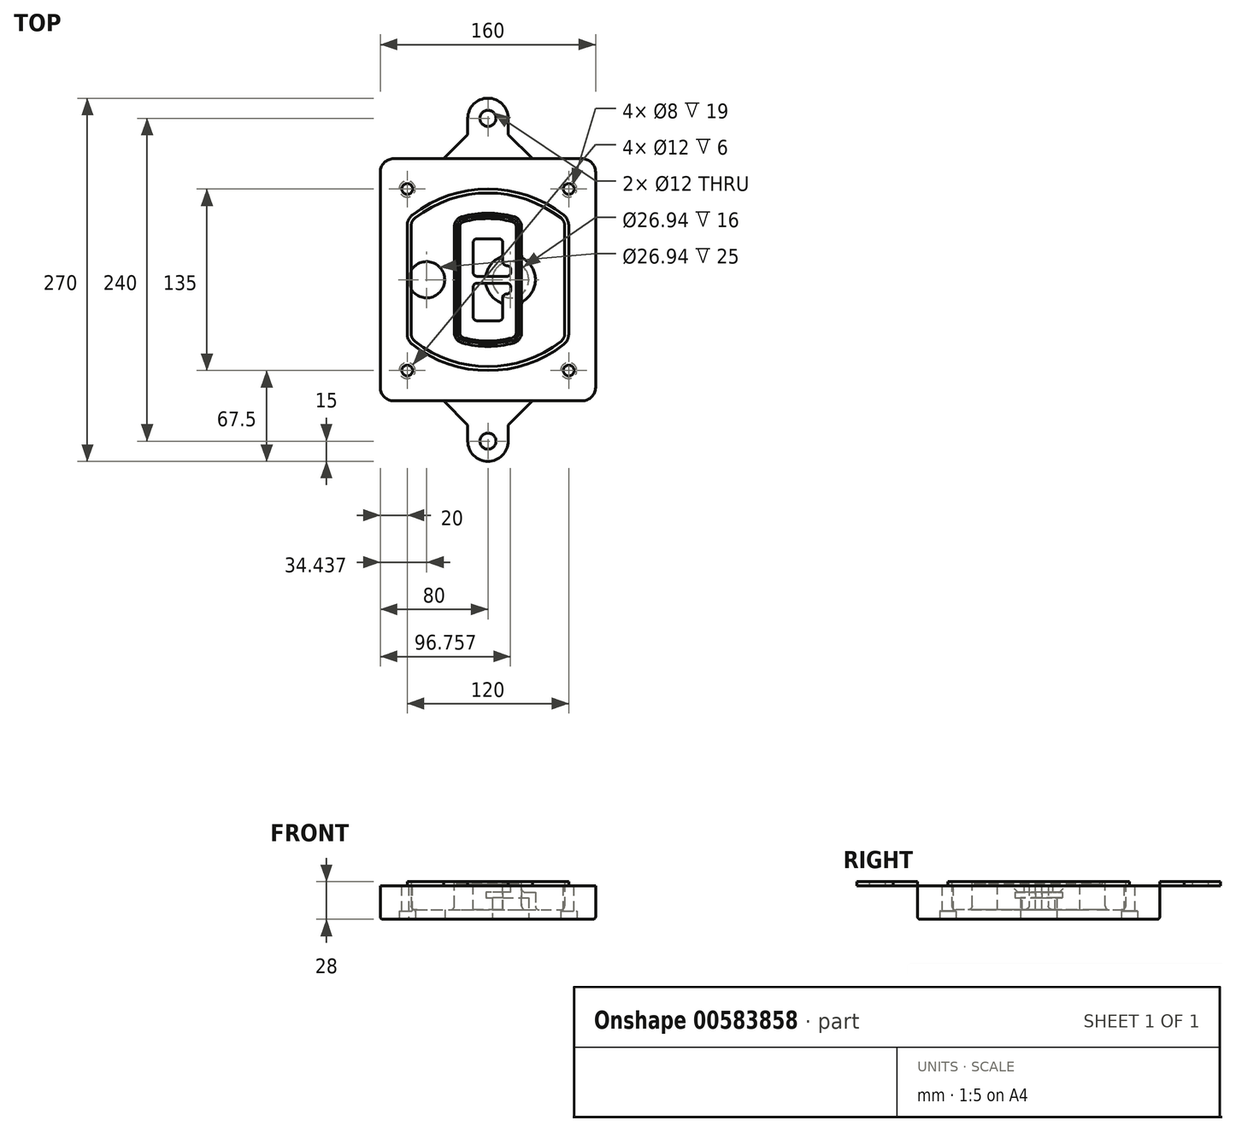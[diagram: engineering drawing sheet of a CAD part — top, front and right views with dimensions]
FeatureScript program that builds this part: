
annotation { "Feature Type Name" : "Feature", "Feature Type Description" : "" }
export const myFeature = defineFeature(function(context is Context, id is Id, definition is map)
    precondition{}
    {
        {
            var Q0;
            Q0=qCreatedBy(makeId("Top.planeOp"),FACE);
            var sketch = newSketch(context, id + "F0", { "sketchPlane" : qUnion([Q0])});
            skPoint(sketch, "E0.rect.middle", {"position": v(0, 0) * mm});
            skLineSegment(sketch, "E1.bottom", {"start": v(-70, -90) * mm, "end": v(70, -90) * mm});
            skLineSegment(sketch, "E1.top", {"start": v(-70, 90) * mm, "end": v(70, 90) * mm});
            skLineSegment(sketch, "E1.left", {"start": v(-80, -80) * mm, "end": v(-80, 80) * mm});
            skLineSegment(sketch, "E1.right", {"start": v(80, -80) * mm, "end": v(80, 80) * mm});
            skLineSegment(sketch, "E2", {"start": v(-80, 90) * mm, "end": v(80, -90) * mm, "construction": true});
            skLineSegment(sketch, "E3", {"start": v(80, 90) * mm, "end": v(-80, -90) * mm, "construction": true});
            skCircle(sketch, "E4", {"center": v(-60, 67.5) * mm, "radius": 4 * mm});
            skCircle(sketch, "E5", {"center": v(60, 67.5) * mm, "radius": 4 * mm});
            skCircle(sketch, "E6", {"center": v(60, -67.5) * mm, "radius": 4 * mm});
            skCircle(sketch, "E7", {"center": v(-60, -67.5) * mm, "radius": 4 * mm});
            skLineSegment(sketch, "E8", {"start": v(-60, 67.5) * mm, "end": v(60, 67.5) * mm, "construction": true});
            skLineSegment(sketch, "E9", {"start": v(60, 67.5) * mm, "end": v(60, -67.5) * mm, "construction": true});
            skLineSegment(sketch, "E10", {"start": v(60, -67.5) * mm, "end": v(-60, -67.5) * mm, "construction": true});
            skLineSegment(sketch, "E11", {"start": v(-60, -67.5) * mm, "end": v(-60, 67.5) * mm, "construction": true});
            skLineSegment(sketch, "E12", {"start": v(-60, 40.3) * mm, "end": v(-60, -40.3) * mm});
            skLineSegment(sketch, "E13", {"start": v(60, 40.3) * mm, "end": v(60, -40.3) * mm});
            skArc(sketch, "E14", {"start": v(56.15, 48.18) * mm, "mid": v(0, 67.5) * mm, "end": v(-56.15, 48.18) * mm});
            skArc(sketch, "E15", {"start": v(-56.15, -48.18) * mm, "mid": v(0, -67.5) * mm, "end": v(56.15, -48.18) * mm});
            skLineSegment(sketch, "E16", {"start": v(-60, 0) * mm, "end": v(60, 0) * mm, "construction": true});
            skPoint(sketch, "E17.visualSharp", {"position": v(-60, -45) * mm});
            skArc(sketch, "E17.filletArc", {"start": v(-60, -40.3) * mm, "mid": v(-58.99, -44.68) * mm, "end": v(-56.15, -48.18) * mm});
            skPoint(sketch, "E18.visualSharp", {"position": v(-60, 45) * mm});
            skArc(sketch, "E18.filletArc", {"start": v(-56.15, 48.18) * mm, "mid": v(-58.99, 44.68) * mm, "end": v(-60, 40.3) * mm});
            skPoint(sketch, "E19.visualSharp", {"position": v(60, 45) * mm});
            skArc(sketch, "E19.filletArc", {"start": v(60, 40.3) * mm, "mid": v(58.99, 44.68) * mm, "end": v(56.15, 48.18) * mm});
            skPoint(sketch, "E20.visualSharp", {"position": v(60, -45) * mm});
            skArc(sketch, "E20.filletArc", {"start": v(56.15, -48.18) * mm, "mid": v(58.99, -44.68) * mm, "end": v(60, -40.3) * mm});
            skPoint(sketch, "E21.visualSharp", {"position": v(-80, 90) * mm});
            skArc(sketch, "E21.filletArc", {"start": v(-70, 90) * mm, "mid": v(-77.07, 87.07) * mm, "end": v(-80, 80) * mm});
            skPoint(sketch, "E22.visualSharp", {"position": v(80, 90) * mm});
            skArc(sketch, "E22.filletArc", {"start": v(80, 80) * mm, "mid": v(77.07, 87.07) * mm, "end": v(70, 90) * mm});
            skPoint(sketch, "E23.visualSharp", {"position": v(80, -90) * mm});
            skArc(sketch, "E23.filletArc", {"start": v(70, -90) * mm, "mid": v(77.07, -87.07) * mm, "end": v(80, -80) * mm});
            skPoint(sketch, "E24.visualSharp", {"position": v(-80, -90) * mm});
            skArc(sketch, "E24.filletArc", {"start": v(-80, -80) * mm, "mid": v(-77.07, -87.07) * mm, "end": v(-70, -90) * mm});
            skArc(sketch, "E25.0", {"start": v(57, 40.3) * mm, "mid": v(56.3, 43.36) * mm, "end": v(54.3, 45.81) * mm});
            skLineSegment(sketch, "E25.1", {"start": v(57, 40.3) * mm, "end": v(57, -40.3) * mm});
            skArc(sketch, "E25.2", {"start": v(54.3, -45.81) * mm, "mid": v(56.3, -43.36) * mm, "end": v(57, -40.3) * mm});
            skArc(sketch, "E25.3", {"start": v(-54.3, -45.81) * mm, "mid": v(0, -64.5) * mm, "end": v(54.3, -45.81) * mm});
            skArc(sketch, "E25.4", {"start": v(-57, -40.3) * mm, "mid": v(-56.3, -43.36) * mm, "end": v(-54.3, -45.81) * mm});
            skArc(sketch, "E25.5", {"start": v(54.3, 45.81) * mm, "mid": v(0, 64.5) * mm, "end": v(-54.3, 45.81) * mm});
            skLineSegment(sketch, "E25.6", {"start": v(-57, 40.3) * mm, "end": v(-57, -40.3) * mm});
            skArc(sketch, "E25.7", {"start": v(-54.3, 45.81) * mm, "mid": v(-56.3, 43.36) * mm, "end": v(-57, 40.3) * mm});
            skArc(sketch, "E26.0", {"start": v(-58.62, 51.33) * mm, "mid": v(-62.58, 46.43) * mm, "end": v(-64, 40.3) * mm});
            skArc(sketch, "E26.1", {"start": v(58.62, 51.33) * mm, "mid": v(0, 71.5) * mm, "end": v(-58.62, 51.33) * mm});
            skArc(sketch, "E26.2", {"start": v(64, 40.3) * mm, "mid": v(62.58, 46.43) * mm, "end": v(58.62, 51.33) * mm});
            skLineSegment(sketch, "E26.3", {"start": v(64, 40.3) * mm, "end": v(64, -40.3) * mm});
            skArc(sketch, "E26.4", {"start": v(58.62, -51.33) * mm, "mid": v(62.58, -46.43) * mm, "end": v(64, -40.3) * mm});
            skLineSegment(sketch, "E26.5", {"start": v(-64, 40.3) * mm, "end": v(-64, -40.3) * mm});
            skArc(sketch, "E26.6", {"start": v(-58.62, -51.33) * mm, "mid": v(0, -71.5) * mm, "end": v(58.62, -51.33) * mm});
            skArc(sketch, "E26.7", {"start": v(-64, -40.3) * mm, "mid": v(-62.58, -46.43) * mm, "end": v(-58.62, -51.33) * mm});
            skSolve(sketch);
        }
        {
            var Q0;
            Q0=makeQuery(id+"F0.imprint","IMPRINT",FACE,{"disambiguationData":[TD([[makeQuery(id+"F0.imprint","IMPRINT",EDGE,{"derivedFrom":sQuery(id+"F0.wireOp",EDGE,"E1.bottom")}),1.0]])]});
            var Q1;
            Q1=makeQuery(id+"F0.imprint","IMPRINT",FACE,{"disambiguationData":[TD([[makeQuery(id+"F0.imprint","IMPRINT",EDGE,{"derivedFrom":sQuery(id+"F0.wireOp",EDGE,"E12")}),1.0]])]});
            var Q2;
            Q2=makeQuery(id+"F0.imprint","IMPRINT",FACE,{"disambiguationData":[TD([[makeQuery(id+"F0.imprint","IMPRINT",EDGE,{"derivedFrom":sQuery(id+"F0.wireOp",EDGE,"E25.0")}),1.0]])]});
            var Q3;
            Q3=makeQuery(id+"F0.imprint","IMPRINT",FACE,{"disambiguationData":[TD([[makeQuery(id+"F0.imprint","IMPRINT",EDGE,{"derivedFrom":sQuery(id+"F0.wireOp",EDGE,"E12")}),-1.0]])]});
            extrude(context, id + "F1", {"entities" : qUnion([Q0, Q1, Q2, Q3]), "oppositeDirection" : true, "depth" : 25 * mm});
        }
        {
            var Q0;
            Q0=makeQuery(id+"F0.imprint","IMPRINT",FACE,{"disambiguationData":[TD([[makeQuery(id+"F0.imprint","IMPRINT",EDGE,{"derivedFrom":sQuery(id+"F0.wireOp",EDGE,"E12")}),1.0]])]});
            extrude(context, id + "F2", {"entities" : qUnion([Q0]), "operationType" : NewBodyOperationType.ADD, "depth" : 3 * mm});
        }
        {
            var Q0;
            Q0=makeQuery(id+"F0.imprint","IMPRINT",FACE,{"disambiguationData":[TD([[makeQuery(id+"F0.imprint","IMPRINT",EDGE,{"derivedFrom":sQuery(id+"F0.wireOp",EDGE,"E25.0")}),1.0]])]});
            extrude(context, id + "F3", {"entities" : qUnion([Q0]), "operationType" : NewBodyOperationType.REMOVE, "oppositeDirection" : true, "depth" : 18 * mm});
        }
        {
            var Q0;
            Q0=makeQuery(id+"F2.opExtrude","CAP_FACE",FACE,{"disambiguationData":[OSD([sQuery(id+"F0.wireOp",EDGE,"E12"),sQuery(id+"F0.wireOp",EDGE,"E13"),sQuery(id+"F0.wireOp",EDGE,"E14"),sQuery(id+"F0.wireOp",EDGE,"E15"),sQuery(id+"F0.wireOp",EDGE,"E17.filletArc"),sQuery(id+"F0.wireOp",EDGE,"E18.filletArc"),sQuery(id+"F0.wireOp",EDGE,"E19.filletArc"),sQuery(id+"F0.wireOp",EDGE,"E20.filletArc"),sQuery(id+"F0.wireOp",EDGE,"E25.0"),sQuery(id+"F0.wireOp",EDGE,"E25.1"),sQuery(id+"F0.wireOp",EDGE,"E25.2"),sQuery(id+"F0.wireOp",EDGE,"E25.3"),sQuery(id+"F0.wireOp",EDGE,"E25.4"),sQuery(id+"F0.wireOp",EDGE,"E25.5"),sQuery(id+"F0.wireOp",EDGE,"E25.6"),sQuery(id+"F0.wireOp",EDGE,"E25.7")])],"isStart":false});
            var sketch = newSketch(context, id + "F4", { "sketchPlane" : qUnion([Q0])});
            skArc(sketch, "E27.0", {"start": v(-19.08, -46.97) * mm, "mid": v(0, -49.5) * mm, "end": v(19.08, -46.97) * mm});
            skArc(sketch, "E28.0", {"start": v(19.08, 46.97) * mm, "mid": v(0, 49.5) * mm, "end": v(-19.08, 46.97) * mm});
            skLineSegment(sketch, "E29", {"start": v(-25, 39.25) * mm, "end": v(-25, -39.25) * mm});
            skLineSegment(sketch, "E30", {"start": v(25, 39.25) * mm, "end": v(25, -39.25) * mm});
            skLineSegment(sketch, "E31", {"start": v(-25, 45.1) * mm, "end": v(25, 45.1) * mm, "construction": true});
            skLineSegment(sketch, "E32", {"start": v(-25, -45.1) * mm, "end": v(25, -45.1) * mm, "construction": true});
            skPoint(sketch, "E33.visualSharp", {"position": v(-25, 45.1) * mm});
            skArc(sketch, "E33.filletArc", {"start": v(-19.08, 46.97) * mm, "mid": v(-23.35, 44.11) * mm, "end": v(-25, 39.25) * mm});
            skPoint(sketch, "E34.visualSharp", {"position": v(25, 45.1) * mm});
            skArc(sketch, "E34.filletArc", {"start": v(25, 39.25) * mm, "mid": v(23.35, 44.11) * mm, "end": v(19.08, 46.97) * mm});
            skPoint(sketch, "E35.visualSharp", {"position": v(25, -45.1) * mm});
            skArc(sketch, "E35.filletArc", {"start": v(19.08, -46.97) * mm, "mid": v(23.35, -44.11) * mm, "end": v(25, -39.25) * mm});
            skPoint(sketch, "E36.visualSharp", {"position": v(-25, -45.1) * mm});
            skArc(sketch, "E36.filletArc", {"start": v(-25, -39.25) * mm, "mid": v(-23.35, -44.11) * mm, "end": v(-19.08, -46.97) * mm});
            skArc(sketch, "E37.0", {"start": v(54.3, 45.81) * mm, "mid": v(0, 64.5) * mm, "end": v(-54.3, 45.81) * mm});
            skArc(sketch, "E37.1", {"start": v(-54.3, 45.81) * mm, "mid": v(-56.3, 43.36) * mm, "end": v(-57, 40.3) * mm});
            skLineSegment(sketch, "E37.2", {"start": v(-57, 40.3) * mm, "end": v(-57, -40.3) * mm});
            skArc(sketch, "E37.3", {"start": v(-57, -40.3) * mm, "mid": v(-56.3, -43.36) * mm, "end": v(-54.3, -45.81) * mm});
            skArc(sketch, "E37.4", {"start": v(-54.3, -45.81) * mm, "mid": v(0, -64.5) * mm, "end": v(54.3, -45.81) * mm});
            skArc(sketch, "E37.5", {"start": v(54.3, -45.81) * mm, "mid": v(56.3, -43.36) * mm, "end": v(57, -40.3) * mm});
            skLineSegment(sketch, "E37.6", {"start": v(57, 40.3) * mm, "end": v(57, -40.3) * mm});
            skArc(sketch, "E37.7", {"start": v(57, 40.3) * mm, "mid": v(56.3, 43.36) * mm, "end": v(54.3, 45.81) * mm});
            skLineSegment(sketch, "E38.0", {"start": v(23, 39.25) * mm, "end": v(23, -39.25) * mm});
            skArc(sketch, "E38.1", {"start": v(18.56, -45.04) * mm, "mid": v(21.76, -42.9) * mm, "end": v(23, -39.25) * mm});
            skArc(sketch, "E38.2", {"start": v(-18.56, -45.04) * mm, "mid": v(0, -47.5) * mm, "end": v(18.56, -45.04) * mm});
            skArc(sketch, "E38.3", {"start": v(-23, -39.25) * mm, "mid": v(-21.76, -42.9) * mm, "end": v(-18.56, -45.04) * mm});
            skLineSegment(sketch, "E38.4", {"start": v(-23, 39.25) * mm, "end": v(-23, -39.25) * mm});
            skArc(sketch, "E38.5", {"start": v(23, 39.25) * mm, "mid": v(21.76, 42.9) * mm, "end": v(18.56, 45.04) * mm});
            skArc(sketch, "E38.6", {"start": v(-18.56, 45.04) * mm, "mid": v(-21.76, 42.9) * mm, "end": v(-23, 39.25) * mm});
            skArc(sketch, "E38.7", {"start": v(18.56, 45.04) * mm, "mid": v(0, 47.5) * mm, "end": v(-18.56, 45.04) * mm});
            skArc(sketch, "E39.0", {"start": v(21, 39.25) * mm, "mid": v(20.18, 41.68) * mm, "end": v(18.04, 43.1) * mm});
            skLineSegment(sketch, "E39.1", {"start": v(21, 39.25) * mm, "end": v(21, -39.25) * mm});
            skArc(sketch, "E39.2", {"start": v(18.04, -43.1) * mm, "mid": v(20.18, -41.68) * mm, "end": v(21, -39.25) * mm});
            skArc(sketch, "E39.3", {"start": v(-18.04, -43.1) * mm, "mid": v(0, -45.5) * mm, "end": v(18.04, -43.1) * mm});
            skArc(sketch, "E39.4", {"start": v(-21, -39.25) * mm, "mid": v(-20.18, -41.68) * mm, "end": v(-18.04, -43.1) * mm});
            skArc(sketch, "E39.5", {"start": v(18.04, 43.1) * mm, "mid": v(0, 45.5) * mm, "end": v(-18.04, 43.1) * mm});
            skLineSegment(sketch, "E39.6", {"start": v(-21, 39.25) * mm, "end": v(-21, -39.25) * mm});
            skArc(sketch, "E39.7", {"start": v(-18.04, 43.1) * mm, "mid": v(-20.18, 41.68) * mm, "end": v(-21, 39.25) * mm});
            skLineSegment(sketch, "E40", {"start": v(-25, 0) * mm, "end": v(25, 0) * mm, "construction": true});
            skLineSegment(sketch, "E41", {"start": v(-11, 5.5) * mm, "end": v(-11, 27.5) * mm});
            skLineSegment(sketch, "E42", {"start": v(-8, 30.5) * mm, "end": v(8, 30.5) * mm});
            skLineSegment(sketch, "E43", {"start": v(11, 27.5) * mm, "end": v(11, 13.5) * mm});
            skLineSegment(sketch, "E44", {"start": v(14, 10.5) * mm, "end": v(14, 10.5) * mm});
            skLineSegment(sketch, "E45", {"start": v(17, 7.5) * mm, "end": v(17, 5.5) * mm});
            skLineSegment(sketch, "E46", {"start": v(14, 2.5) * mm, "end": v(-8, 2.5) * mm});
            skPoint(sketch, "E47.visualSharp", {"position": v(-11, 30.5) * mm});
            skArc(sketch, "E47.filletArc", {"start": v(-8, 30.5) * mm, "mid": v(-10.12, 29.62) * mm, "end": v(-11, 27.5) * mm});
            skPoint(sketch, "E48.visualSharp", {"position": v(11, 30.5) * mm});
            skArc(sketch, "E48.filletArc", {"start": v(11, 27.5) * mm, "mid": v(10.12, 29.62) * mm, "end": v(8, 30.5) * mm});
            skPoint(sketch, "E49.visualSharp", {"position": v(11, 10.5) * mm});
            skArc(sketch, "E49.filletArc", {"start": v(11, 13.5) * mm, "mid": v(11.88, 11.38) * mm, "end": v(14, 10.5) * mm});
            skPoint(sketch, "E50.visualSharp", {"position": v(17, 10.5) * mm});
            skArc(sketch, "E50.filletArc", {"start": v(17, 7.5) * mm, "mid": v(16.12, 9.62) * mm, "end": v(14, 10.5) * mm});
            skPoint(sketch, "E51.visualSharp", {"position": v(17, 2.5) * mm});
            skArc(sketch, "E51.filletArc", {"start": v(14, 2.5) * mm, "mid": v(16.12, 3.38) * mm, "end": v(17, 5.5) * mm});
            skPoint(sketch, "E52.visualSharp", {"position": v(-11, 2.5) * mm});
            skArc(sketch, "E52.filletArc", {"start": v(-11, 5.5) * mm, "mid": v(-10.12, 3.38) * mm, "end": v(-8, 2.5) * mm});
            skLineSegment(sketch, "E53.0.MirrorCS", {"start": v(14, -2.5) * mm, "end": v(-8, -2.5) * mm});
            skArc(sketch, "E54.0.MirrorCS", {"start": v(-11, -5.5) * mm, "mid": v(-10.12, -3.38) * mm, "end": v(-8, -2.5) * mm});
            skLineSegment(sketch, "E55.0.MirrorCS", {"start": v(-11, -5.5) * mm, "end": v(-11, -27.5) * mm});
            skArc(sketch, "E56.0.MirrorCS", {"start": v(-8, -30.5) * mm, "mid": v(-10.12, -29.62) * mm, "end": v(-11, -27.5) * mm});
            skLineSegment(sketch, "E57.0.MirrorCS", {"start": v(-8, -30.5) * mm, "end": v(8, -30.5) * mm});
            skArc(sketch, "E58.0.MirrorCS", {"start": v(11, -27.5) * mm, "mid": v(10.12, -29.62) * mm, "end": v(8, -30.5) * mm});
            skLineSegment(sketch, "E59.0.MirrorCS", {"start": v(11, -27.5) * mm, "end": v(11, -13.5) * mm});
            skArc(sketch, "E60.0.MirrorCS", {"start": v(11, -13.5) * mm, "mid": v(11.88, -11.38) * mm, "end": v(14, -10.5) * mm});
            skArc(sketch, "E61.0.MirrorCS", {"start": v(17, -7.5) * mm, "mid": v(16.12, -9.62) * mm, "end": v(14, -10.5) * mm});
            skLineSegment(sketch, "E62.0.MirrorCS", {"start": v(17, -7.5) * mm, "end": v(17, -5.5) * mm});
            skArc(sketch, "E63.0.MirrorCS", {"start": v(14, -2.5) * mm, "mid": v(16.12, -3.38) * mm, "end": v(17, -5.5) * mm});
            skSolve(sketch);
        }
        {
            var Q0;
            Q0=makeQuery(id+"F4.imprint","IMPRINT",FACE,{"disambiguationData":[TD([[makeQuery(id+"F4.imprint","IMPRINT",EDGE,{"derivedFrom":sQuery(id+"F4.wireOp",EDGE,"E27.0")}),1.0]])]});
            var Q1;
            Q1=makeQuery(id+"F4.imprint","IMPRINT",FACE,{"disambiguationData":[TD([[makeQuery(id+"F4.imprint","IMPRINT",EDGE,{"derivedFrom":sQuery(id+"F4.wireOp",EDGE,"E38.0")}),-1.0]])]});
            var Q2;
            Q2=makeQuery(id+"F4.imprint","IMPRINT",FACE,{"disambiguationData":[TD([[makeQuery(id+"F4.imprint","IMPRINT",EDGE,{"derivedFrom":sQuery(id+"F4.wireOp",EDGE,"E39.0")}),1.0]])]});
            extrude(context, id + "F5", {"entities" : qUnion([Q0, Q1, Q2]), "operationType" : NewBodyOperationType.ADD, "endBound" : BoundingType.UP_TO_NEXT, "oppositeDirection" : true, "depth" : 25 * mm});
        }
        {
            var Q0;
            Q0=makeQuery(id+"F4.imprint","IMPRINT",FACE,{"disambiguationData":[TD([[makeQuery(id+"F4.imprint","IMPRINT",EDGE,{"derivedFrom":sQuery(id+"F4.wireOp",EDGE,"E38.0")}),-1.0]])]});
            extrude(context, id + "F6", {"entities" : qUnion([Q0]), "operationType" : NewBodyOperationType.REMOVE, "oppositeDirection" : true, "depth" : 2 * mm});
        }
        {
            var Q0;
            Q0=makeQuery(id+"F1.opExtrude","CAP_FACE",FACE,{"disambiguationData":[OSD([sQuery(id+"F0.wireOp",EDGE,"E1.bottom"),sQuery(id+"F0.wireOp",EDGE,"E1.top"),sQuery(id+"F0.wireOp",EDGE,"E1.left"),sQuery(id+"F0.wireOp",EDGE,"E1.right"),sQuery(id+"F0.wireOp",EDGE,"E4"),sQuery(id+"F0.wireOp",EDGE,"E5"),sQuery(id+"F0.wireOp",EDGE,"E6"),sQuery(id+"F0.wireOp",EDGE,"E7"),sQuery(id+"F0.wireOp",EDGE,"E21.filletArc"),sQuery(id+"F0.wireOp",EDGE,"E22.filletArc"),sQuery(id+"F0.wireOp",EDGE,"E23.filletArc"),sQuery(id+"F0.wireOp",EDGE,"E24.filletArc")])],"isStart":false});
            var sketch = newSketch(context, id + "F7", { "sketchPlane" : qUnion([Q0])});
            skCircle(sketch, "E64", {"center": v(16.76, 0) * mm, "radius": 13.47 * mm});
            skCircle(sketch, "E65", {"center": v(-45.56, 0) * mm, "radius": 13.47 * mm});
            skLineSegment(sketch, "E66", {"start": v(80, 0) * mm, "end": v(-80, 0) * mm});
            skCircle(sketch, "E67", {"center": v(16.76, 0) * mm, "radius": 18.47 * mm});
            skCircle(sketch, "E68", {"center": v(60, -67.5) * mm, "radius": 6 * mm});
            skCircle(sketch, "E69", {"center": v(-60, -67.5) * mm, "radius": 6 * mm});
            skCircle(sketch, "E70", {"center": v(-60, 67.5) * mm, "radius": 6 * mm});
            skCircle(sketch, "E71", {"center": v(60, 67.5) * mm, "radius": 6 * mm});
            skSolve(sketch);
        }
        {
            var Q0;
            {var subQ1=sQuery(id+"F7.wireOp",EDGE,"E66");var subQ4=sQuery(id+"F7.wireOp",EDGE,"E64");var subQ6=makeQuery(id+"F7.imprint","INTERSECT",VERTEX,{"disambiguationData":[OD(0.0)],"derivedFrom":[subQ4,subQ1]});Q0=makeQuery(id+"F7.imprint","IMPRINT",FACE,{"disambiguationData":[TD([[makeQuery(id+"F7.imprint","IMPRINT",EDGE,{"disambiguationData":[TD([[subQ6,-1.0]])],"derivedFrom":subQ4}),-1.0]])]});}
            var Q1;
            {var subQ0=sQuery(id+"F7.wireOp",EDGE,"E66");var subQ1=sQuery(id+"F7.wireOp",EDGE,"E64");var subQ3=makeQuery(id+"F7.imprint","INTERSECT",VERTEX,{"disambiguationData":[OD(0.0)],"derivedFrom":[subQ1,subQ0]});Q1=makeQuery(id+"F7.imprint","IMPRINT",FACE,{"disambiguationData":[TD([[makeQuery(id+"F7.imprint","IMPRINT",EDGE,{"disambiguationData":[TD([[subQ3,-1.0]])],"derivedFrom":subQ1}),1.0]])]});}
            var Q2;
            {var subQ0=sQuery(id+"F7.wireOp",EDGE,"E66");var subQ1=sQuery(id+"F7.wireOp",EDGE,"E64");var subQ3=makeQuery(id+"F7.imprint","INTERSECT",VERTEX,{"disambiguationData":[OD(0.0)],"derivedFrom":[subQ1,subQ0]});Q2=makeQuery(id+"F7.imprint","IMPRINT",FACE,{"disambiguationData":[TD([[makeQuery(id+"F7.imprint","IMPRINT",EDGE,{"disambiguationData":[TD([[subQ3,1.0]])],"derivedFrom":subQ1}),1.0]])]});}
            var Q3;
            {var subQ1=sQuery(id+"F7.wireOp",EDGE,"E66");var subQ4=sQuery(id+"F7.wireOp",EDGE,"E64");var subQ6=makeQuery(id+"F7.imprint","INTERSECT",VERTEX,{"disambiguationData":[OD(0.0)],"derivedFrom":[subQ4,subQ1]});Q3=makeQuery(id+"F7.imprint","IMPRINT",FACE,{"disambiguationData":[TD([[makeQuery(id+"F7.imprint","IMPRINT",EDGE,{"disambiguationData":[TD([[subQ6,1.0]])],"derivedFrom":subQ4}),-1.0]])]});}
            extrude(context, id + "F8", {"entities" : qUnion([Q0, Q1, Q2, Q3]), "operationType" : NewBodyOperationType.ADD, "oppositeDirection" : true, "depth" : 20 * mm});
        }
        {
            var Q0;
            {var subQ0=sQuery(id+"F7.wireOp",EDGE,"E66");var subQ1=sQuery(id+"F7.wireOp",EDGE,"E64");var subQ3=makeQuery(id+"F7.imprint","INTERSECT",VERTEX,{"disambiguationData":[OD(0.0)],"derivedFrom":[subQ1,subQ0]});Q0=makeQuery(id+"F7.imprint","IMPRINT",FACE,{"disambiguationData":[TD([[makeQuery(id+"F7.imprint","IMPRINT",EDGE,{"disambiguationData":[TD([[subQ3,-1.0]])],"derivedFrom":subQ1}),1.0]])]});}
            var Q1;
            {var subQ0=sQuery(id+"F7.wireOp",EDGE,"E66");var subQ1=sQuery(id+"F7.wireOp",EDGE,"E64");var subQ3=makeQuery(id+"F7.imprint","INTERSECT",VERTEX,{"disambiguationData":[OD(0.0)],"derivedFrom":[subQ1,subQ0]});Q1=makeQuery(id+"F7.imprint","IMPRINT",FACE,{"disambiguationData":[TD([[makeQuery(id+"F7.imprint","IMPRINT",EDGE,{"disambiguationData":[TD([[subQ3,1.0]])],"derivedFrom":subQ1}),1.0]])]});}
            extrude(context, id + "F9", {"entities" : qUnion([Q0, Q1]), "operationType" : NewBodyOperationType.REMOVE, "oppositeDirection" : true, "depth" : 16 * mm});
        }
        {
            var Q0;
            {var subQ0=sQuery(id+"F7.wireOp",EDGE,"E66");var subQ1=sQuery(id+"F7.wireOp",EDGE,"E65");var subQ3=makeQuery(id+"F7.imprint","INTERSECT",VERTEX,{"disambiguationData":[OD(0.0)],"derivedFrom":[subQ1,subQ0]});Q0=makeQuery(id+"F7.imprint","IMPRINT",FACE,{"disambiguationData":[TD([[makeQuery(id+"F7.imprint","IMPRINT",EDGE,{"disambiguationData":[TD([[subQ3,-1.0]])],"derivedFrom":subQ1}),1.0]])]});}
            var Q1;
            {var subQ0=sQuery(id+"F7.wireOp",EDGE,"E66");var subQ1=sQuery(id+"F7.wireOp",EDGE,"E65");var subQ3=makeQuery(id+"F7.imprint","INTERSECT",VERTEX,{"disambiguationData":[OD(0.0)],"derivedFrom":[subQ1,subQ0]});Q1=makeQuery(id+"F7.imprint","IMPRINT",FACE,{"disambiguationData":[TD([[makeQuery(id+"F7.imprint","IMPRINT",EDGE,{"disambiguationData":[TD([[subQ3,1.0]])],"derivedFrom":subQ1}),1.0]])]});}
            extrude(context, id + "F10", {"entities" : qUnion([Q0, Q1]), "operationType" : NewBodyOperationType.REMOVE, "oppositeDirection" : true, "depth" : 25 * mm});
        }
        {
            var Q0;
            Q0=makeQuery(id+"F7.imprint","IMPRINT",FACE,{"disambiguationData":[TD([[makeQuery(id+"F7.imprint","IMPRINT",EDGE,{"derivedFrom":sQuery(id+"F7.wireOp",EDGE,"E68")}),1.0]])]});
            var Q1;
            Q1=makeQuery(id+"F7.imprint","IMPRINT",FACE,{"disambiguationData":[TD([[makeQuery(id+"F7.imprint","IMPRINT",EDGE,{"derivedFrom":makeQuery(id+"F1.opExtrude","CAP_EDGE",EDGE,{"disambiguationData":[OSD([sQuery(id+"F0.wireOp",EDGE,"E5")])],"isStart":false})}),-1.0]])]});
            var Q2;
            Q2=makeQuery(id+"F7.imprint","IMPRINT",FACE,{"disambiguationData":[TD([[makeQuery(id+"F7.imprint","IMPRINT",EDGE,{"derivedFrom":sQuery(id+"F7.wireOp",EDGE,"E69")}),1.0]])]});
            var Q3;
            Q3=makeQuery(id+"F7.imprint","IMPRINT",FACE,{"disambiguationData":[TD([[makeQuery(id+"F7.imprint","IMPRINT",EDGE,{"derivedFrom":makeQuery(id+"F1.opExtrude","CAP_EDGE",EDGE,{"disambiguationData":[OSD([sQuery(id+"F0.wireOp",EDGE,"E4")])],"isStart":false})}),-1.0]])]});
            var Q4;
            Q4=makeQuery(id+"F7.imprint","IMPRINT",FACE,{"disambiguationData":[TD([[makeQuery(id+"F7.imprint","IMPRINT",EDGE,{"derivedFrom":sQuery(id+"F7.wireOp",EDGE,"E70")}),1.0]])]});
            var Q5;
            Q5=makeQuery(id+"F7.imprint","IMPRINT",FACE,{"disambiguationData":[TD([[makeQuery(id+"F7.imprint","IMPRINT",EDGE,{"derivedFrom":makeQuery(id+"F1.opExtrude","CAP_EDGE",EDGE,{"disambiguationData":[OSD([sQuery(id+"F0.wireOp",EDGE,"E7")])],"isStart":false})}),-1.0]])]});
            var Q6;
            Q6=makeQuery(id+"F7.imprint","IMPRINT",FACE,{"disambiguationData":[TD([[makeQuery(id+"F7.imprint","IMPRINT",EDGE,{"derivedFrom":sQuery(id+"F7.wireOp",EDGE,"E71")}),1.0]])]});
            var Q7;
            Q7=makeQuery(id+"F7.imprint","IMPRINT",FACE,{"disambiguationData":[TD([[makeQuery(id+"F7.imprint","IMPRINT",EDGE,{"derivedFrom":makeQuery(id+"F1.opExtrude","CAP_EDGE",EDGE,{"disambiguationData":[OSD([sQuery(id+"F0.wireOp",EDGE,"E6")])],"isStart":false})}),-1.0]])]});
            extrude(context, id + "F11", {"entities" : qUnion([Q0, Q1, Q2, Q3, Q4, Q5, Q6, Q7]), "operationType" : NewBodyOperationType.REMOVE, "oppositeDirection" : true, "depth" : 6 * mm});
        }
        {
            var Q0;
            Q0=makeQuery(id+"F9.boolean.opBoolean","COPY",FACE,{"derivedFrom":makeQuery(id+"F9.opExtrude","CAP_FACE",FACE,{"disambiguationData":[OSD([sQuery(id+"F7.wireOp",EDGE,"E64")])],"isStart":false})});
            var sketch = newSketch(context, id + "F12", { "sketchPlane" : qUnion([Q0])});
            skArc(sketch, "E72.0", {"start": v(11, 17.55) * mm, "mid": v(2.57, 11.82) * mm, "end": v(-1.54, 2.5) * mm});
            skArc(sketch, "E72.1", {"start": v(-1.54, -2.5) * mm, "mid": v(2.57, -11.82) * mm, "end": v(11, -17.55) * mm});
            skLineSegment(sketch, "E73", {"start": v(-1.54, -2.5) * mm, "end": v(14, -2.5) * mm});
            skLineSegment(sketch, "E74.0", {"start": v(14, 2.5) * mm, "end": v(-1.54, 2.5) * mm});
            skArc(sketch, "E74.1", {"start": v(14, 2.5) * mm, "mid": v(16.12, 3.38) * mm, "end": v(17, 5.5) * mm});
            skLineSegment(sketch, "E74.2", {"start": v(17, 7.5) * mm, "end": v(17, 5.5) * mm});
            skArc(sketch, "E74.3", {"start": v(17, 7.5) * mm, "mid": v(16.12, 9.62) * mm, "end": v(14, 10.5) * mm});
            skArc(sketch, "E74.4", {"start": v(11, 13.5) * mm, "mid": v(11.88, 11.38) * mm, "end": v(14, 10.5) * mm});
            skLineSegment(sketch, "E74.5", {"start": v(11, 17.55) * mm, "end": v(11, 13.5) * mm});
            skLineSegment(sketch, "E74.7", {"start": v(14, -2.5) * mm, "end": v(-1.54, -2.5) * mm});
            skArc(sketch, "E74.8", {"start": v(14, -2.5) * mm, "mid": v(16.12, -3.38) * mm, "end": v(17, -5.5) * mm});
            skLineSegment(sketch, "E74.9", {"start": v(17, -7.5) * mm, "end": v(17, -5.5) * mm});
            skArc(sketch, "E74.10", {"start": v(17, -7.5) * mm, "mid": v(16.12, -9.62) * mm, "end": v(14, -10.5) * mm});
            skArc(sketch, "E74.11", {"start": v(11, -13.5) * mm, "mid": v(11.88, -11.38) * mm, "end": v(14, -10.5) * mm});
            skLineSegment(sketch, "E74.12", {"start": v(11, -17.55) * mm, "end": v(11, -13.5) * mm});
            skPoint(sketch, "E75.orphan", {"position": v(11, -27.5) * mm});
            skPoint(sketch, "E76.orphan", {"position": v(-8, -2.5) * mm});
            skPoint(sketch, "E77.orphan", {"position": v(-8, 2.5) * mm});
            skPoint(sketch, "E78.orphan", {"position": v(11, 27.5) * mm});
            skSolve(sketch);
        }
        {
            var Q0;
            {var subQ7=sQuery(id+"F12.wireOp",EDGE,"E72.0");var subQ14=sQuery(id+"F12.wireOp",EDGE,"E72.1");var subQ16=sQuery(id+"F12.wireOp",EDGE,"E74.1");var subQ18=sQuery(id+"F12.wireOp",EDGE,"E74.8");Q0=qUnion([makeQuery(id+"F12.imprint","IMPRINT",FACE,{"disambiguationData":[TD([[makeQuery(id+"F12.imprint","IMPRINT",EDGE,{"derivedFrom":subQ7}),1.0]])]}),makeQuery(id+"F12.imprint","IMPRINT",FACE,{"disambiguationData":[TD([[makeQuery(id+"F12.imprint","IMPRINT",EDGE,{"derivedFrom":subQ14}),1.0]])]}),makeQuery(id+"F12.imprint","IMPRINT",FACE,{"disambiguationData":[TD([[makeQuery(id+"F12.imprint","IMPRINT",EDGE,{"derivedFrom":subQ16}),1.0]])]}),makeQuery(id+"F12.imprint","IMPRINT",FACE,{"disambiguationData":[TD([[makeQuery(id+"F12.imprint","IMPRINT",EDGE,{"derivedFrom":subQ18}),-1.0]])]})]);}
            var Q1;
            Q1=makeQuery(id+"F5.boolean.opBoolean","SPLIT",FACE,{"disambiguationData":[TD([makeQuery(id+"F5.opExtrude","SWEPT_FACE",FACE,{"disambiguationData":[OSD([sQuery(id+"F4.wireOp",EDGE,"E41")])]})])],"derivedFrom":makeQuery(id+"F3.boolean.opBoolean","COPY",FACE,{"derivedFrom":makeQuery(id+"F3.opExtrude","CAP_FACE",FACE,{"disambiguationData":[OSD([sQuery(id+"F0.wireOp",EDGE,"E25.0"),sQuery(id+"F0.wireOp",EDGE,"E25.1"),sQuery(id+"F0.wireOp",EDGE,"E25.2"),sQuery(id+"F0.wireOp",EDGE,"E25.3"),sQuery(id+"F0.wireOp",EDGE,"E25.4"),sQuery(id+"F0.wireOp",EDGE,"E25.5"),sQuery(id+"F0.wireOp",EDGE,"E25.6"),sQuery(id+"F0.wireOp",EDGE,"E25.7")])],"isStart":false})})});
            extrude(context, id + "F13", {"entities" : qUnion([Q0]), "operationType" : NewBodyOperationType.REMOVE, "endBound" : BoundingType.UP_TO_SURFACE, "endBoundEntityFace" : qUnion([Q1]), "depth" : 25 * mm});
        }
        {
            var Q0;
            Q0=makeQuery(id+"F3.boolean.opBoolean","COPY",EDGE,{"derivedFrom":makeQuery(id+"F3.opExtrude","CAP_EDGE",EDGE,{"disambiguationData":[OSD([sQuery(id+"F0.wireOp",EDGE,"E25.6")])],"isStart":false})});
            var Q1;
            Q1=makeQuery(id+"F8.boolean.opBoolean","INTERSECT",EDGE,{"derivedFrom":[makeQuery(id+"F5.opExtrude","SWEPT_FACE",FACE,{"disambiguationData":[OSD([sQuery(id+"F4.wireOp",EDGE,"E30")])]}),makeQuery(id+"F8.opExtrude","CAP_FACE",FACE,{"disambiguationData":[OSD([sQuery(id+"F7.wireOp",EDGE,"E67")])],"isStart":false})]});
            var Q2;
            Q2=makeQuery(id+"F8.boolean.opBoolean","INTERSECT",EDGE,{"disambiguationData":[OD(1.0)],"derivedFrom":[makeQuery(id+"F5.opExtrude","SWEPT_FACE",FACE,{"disambiguationData":[OSD([sQuery(id+"F4.wireOp",EDGE,"E30")])]}),makeQuery(id+"F8.opExtrude","SWEPT_FACE",FACE,{"disambiguationData":[OSD([sQuery(id+"F7.wireOp",EDGE,"E67")])]})]});
            var Q3;
            {var subQ0=sQuery(id+"F4.wireOp",EDGE,"E30");Q3=makeQuery(id+"F8.boolean.opBoolean","SPLIT",EDGE,{"disambiguationData":[TD([makeQuery(id+"F5.opExtrude","SWEPT_FACE",FACE,{"disambiguationData":[OSD([sQuery(id+"F4.wireOp",EDGE,"E35.filletArc")])]})])],"derivedFrom":makeQuery(id+"F5.opExtrude","CAP_EDGE",EDGE,{"disambiguationData":[OSD([subQ0])],"isStart":false})});}
            var Q4;
            {var subQ0=sQuery(id+"F0.wireOp",EDGE,"E25.7");var subQ1=sQuery(id+"F0.wireOp",EDGE,"E25.1");var subQ2=sQuery(id+"F0.wireOp",EDGE,"E25.6");var subQ3=sQuery(id+"F0.wireOp",EDGE,"E25.5");var subQ4=sQuery(id+"F0.wireOp",EDGE,"E25.4");var subQ5=sQuery(id+"F0.wireOp",EDGE,"E25.0");var subQ6=sQuery(id+"F0.wireOp",EDGE,"E25.2");var subQ7=sQuery(id+"F0.wireOp",EDGE,"E25.3");Q4=makeQuery(id+"F8.boolean.opBoolean","INTERSECT",EDGE,{"derivedFrom":[makeQuery(id+"F5.boolean.opBoolean","SPLIT",FACE,{"disambiguationData":[TD([makeQuery(id+"F2.opExtrude","SWEPT_FACE",FACE,{"disambiguationData":[OSD([subQ5])]})])],"derivedFrom":makeQuery(id+"F3.boolean.opBoolean","COPY",FACE,{"derivedFrom":makeQuery(id+"F3.opExtrude","CAP_FACE",FACE,{"disambiguationData":[OSD([subQ5,subQ1,subQ6,subQ7,subQ4,subQ3,subQ2,subQ0])],"isStart":false})})}),makeQuery(id+"F8.opExtrude","SWEPT_FACE",FACE,{"disambiguationData":[OSD([sQuery(id+"F7.wireOp",EDGE,"E67")])]})]});}
            var Q5;
            Q5=makeQuery(id+"F8.boolean.opBoolean","INTERSECT",EDGE,{"disambiguationData":[OD(0.0)],"derivedFrom":[makeQuery(id+"F5.opExtrude","SWEPT_FACE",FACE,{"disambiguationData":[OSD([sQuery(id+"F4.wireOp",EDGE,"E30")])]}),makeQuery(id+"F8.opExtrude","SWEPT_FACE",FACE,{"disambiguationData":[OSD([sQuery(id+"F7.wireOp",EDGE,"E67")])]})]});
            fillet(context, id + "F14", {"entities" : qUnion([Q0, Q1, Q2, Q3, Q4, Q5]), "radius" : 3 * mm, "tangentPropagation" : true, "allowEdgeOverflow" : false});
        }
        {
            var Q0;
            Q0=makeQuery(id+"F1.opExtrude","CAP_EDGE",EDGE,{"disambiguationData":[OSD([sQuery(id+"F0.wireOp",EDGE,"E1.bottom")])],"isStart":false});
            fillet(context, id + "F15", {"entities" : qUnion([Q0]), "radius" : 2 * mm, "tangentPropagation" : true, "allowEdgeOverflow" : false});
        }
        {
            var Q0;
            {var subQ0=sQuery(id+"F0.wireOp",EDGE,"E21.filletArc");var subQ1=sQuery(id+"F0.wireOp",EDGE,"E7");var subQ2=sQuery(id+"F0.wireOp",EDGE,"E6");var subQ3=sQuery(id+"F0.wireOp",EDGE,"E5");var subQ4=sQuery(id+"F0.wireOp",EDGE,"E4");var subQ5=sQuery(id+"F0.wireOp",EDGE,"E22.filletArc");var subQ6=sQuery(id+"F0.wireOp",EDGE,"E1.bottom");var subQ7=sQuery(id+"F0.wireOp",EDGE,"E1.right");var subQ8=sQuery(id+"F0.wireOp",EDGE,"E1.top");var subQ9=sQuery(id+"F0.wireOp",EDGE,"E1.left");var subQ10=sQuery(id+"F0.wireOp",EDGE,"E23.filletArc");var subQ11=sQuery(id+"F0.wireOp",EDGE,"E24.filletArc");Q0=makeQuery(id+"F2.boolean.opBoolean","SPLIT",FACE,{"disambiguationData":[TD([makeQuery(id+"F1.opExtrude","SWEPT_FACE",FACE,{"disambiguationData":[OSD([subQ6])]})])],"derivedFrom":makeQuery(id+"F1.opExtrude","CAP_FACE",FACE,{"disambiguationData":[OSD([subQ6,subQ8,subQ9,subQ7,subQ4,subQ3,subQ2,subQ1,subQ0,subQ5,subQ10,subQ11])],"isStart":true})});}
            var sketch = newSketch(context, id + "F16", { "sketchPlane" : qUnion([Q0])});
            skLineSegment(sketch, "E79.0", {"start": v(-70, 90) * mm, "end": v(70, 90) * mm});
            skArc(sketch, "E79.1", {"start": v(-70, 90) * mm, "mid": v(-77.07, 87.07) * mm, "end": v(-80, 80) * mm});
            skLineSegment(sketch, "E79.2", {"start": v(-80, -80) * mm, "end": v(-80, 80) * mm});
            skArc(sketch, "E79.3", {"start": v(-80, -80) * mm, "mid": v(-77.07, -87.07) * mm, "end": v(-70, -90) * mm});
            skLineSegment(sketch, "E79.4", {"start": v(-70, -90) * mm, "end": v(70, -90) * mm});
            skArc(sketch, "E79.5", {"start": v(70, -90) * mm, "mid": v(77.07, -87.07) * mm, "end": v(80, -80) * mm});
            skLineSegment(sketch, "E79.6", {"start": v(80, -80) * mm, "end": v(80, 80) * mm});
            skArc(sketch, "E79.7", {"start": v(56.15, 48.18) * mm, "mid": v(0, 67.5) * mm, "end": v(-56.15, 48.18) * mm});
            skArc(sketch, "E79.8", {"start": v(60, 40.3) * mm, "mid": v(58.99, 44.68) * mm, "end": v(56.15, 48.18) * mm});
            skCircle(sketch, "E79.9", {"center": v(60, 67.5) * mm, "radius": 4 * mm});
            skArc(sketch, "E79.10", {"start": v(80, 80) * mm, "mid": v(77.07, 87.07) * mm, "end": v(70, 90) * mm});
            skCircle(sketch, "E79.11", {"center": v(-60, 67.5) * mm, "radius": 4 * mm});
            skLineSegment(sketch, "E79.12", {"start": v(-60, 40.3) * mm, "end": v(-60, -40.3) * mm});
            skArc(sketch, "E79.13", {"start": v(-56.15, 48.18) * mm, "mid": v(-58.99, 44.68) * mm, "end": v(-60, 40.3) * mm});
            skArc(sketch, "E79.14", {"start": v(-60, -40.3) * mm, "mid": v(-58.99, -44.68) * mm, "end": v(-56.15, -48.18) * mm});
            skArc(sketch, "E79.15", {"start": v(-56.15, -48.18) * mm, "mid": v(0, -67.5) * mm, "end": v(56.15, -48.18) * mm});
            skLineSegment(sketch, "E79.16", {"start": v(60, 40.3) * mm, "end": v(60, -40.3) * mm});
            skArc(sketch, "E79.17", {"start": v(56.15, -48.18) * mm, "mid": v(58.99, -44.68) * mm, "end": v(60, -40.3) * mm});
            skCircle(sketch, "E79.18", {"center": v(60, -67.5) * mm, "radius": 4 * mm});
            skCircle(sketch, "E79.19", {"center": v(-60, -67.5) * mm, "radius": 4 * mm});
            skLineSegment(sketch, "E80", {"start": v(0, 90) * mm, "end": v(0, 120) * mm, "construction": true});
            skCircle(sketch, "E81", {"center": v(0, 120) * mm, "radius": 6 * mm});
            skLineSegment(sketch, "E82", {"start": v(-33, 90) * mm, "end": v(-15, 108) * mm});
            skLineSegment(sketch, "E83", {"start": v(-15, 108) * mm, "end": v(-15, 120) * mm});
            skLineSegment(sketch, "E84", {"start": v(15, 120) * mm, "end": v(15, 108) * mm});
            skLineSegment(sketch, "E85", {"start": v(15, 108) * mm, "end": v(33, 90) * mm});
            skArc(sketch, "E86", {"start": v(15, 120) * mm, "mid": v(0, 135) * mm, "end": v(-15, 120) * mm});
            skLineSegment(sketch, "E87", {"start": v(-80, 0) * mm, "end": v(80, 0) * mm, "construction": true});
            skLineSegment(sketch, "E88.MirrorCS", {"start": v(0, -90) * mm, "end": v(0, -120) * mm, "construction": true});
            skLineSegment(sketch, "E89.MirrorCS", {"start": v(-33, -90) * mm, "end": v(-15, -108) * mm});
            skLineSegment(sketch, "E90.MirrorCS", {"start": v(15, -120) * mm, "end": v(15, -108) * mm});
            skArc(sketch, "E91.MirrorCS", {"start": v(15, -120) * mm, "mid": v(0, -135) * mm, "end": v(-15, -120) * mm});
            skLineSegment(sketch, "E92.MirrorCS", {"start": v(15, -108) * mm, "end": v(33, -90) * mm});
            skCircle(sketch, "E93.MirrorC", {"center": v(0, -120) * mm, "radius": 6 * mm});
            skLineSegment(sketch, "E94.MirrorCS", {"start": v(-15, -108) * mm, "end": v(-15, -120) * mm});
            skSolve(sketch);
        }
        {
            var Q0;
            Q0=makeQuery(id+"F16.imprint","IMPRINT",FACE,{"disambiguationData":[TD([[makeQuery(id+"F16.imprint","IMPRINT",EDGE,{"derivedFrom":sQuery(id+"F16.wireOp",EDGE,"E81")}),-1.0]])]});
            var Q1;
            {var subQ1=sQuery(id+"F16.wireOp",EDGE,"E89.MirrorCS");Q1=makeQuery(id+"F16.imprint","IMPRINT",FACE,{"disambiguationData":[TD([[makeQuery(id+"F16.imprint","IMPRINT",EDGE,{"derivedFrom":subQ1}),1.0]])]});}
            var Q2;
            Q2=makeQuery(id+"F2.opExtrude","CAP_FACE",FACE,{"disambiguationData":[OSD([sQuery(id+"F0.wireOp",EDGE,"E12"),sQuery(id+"F0.wireOp",EDGE,"E13"),sQuery(id+"F0.wireOp",EDGE,"E14"),sQuery(id+"F0.wireOp",EDGE,"E15"),sQuery(id+"F0.wireOp",EDGE,"E17.filletArc"),sQuery(id+"F0.wireOp",EDGE,"E18.filletArc"),sQuery(id+"F0.wireOp",EDGE,"E19.filletArc"),sQuery(id+"F0.wireOp",EDGE,"E20.filletArc"),sQuery(id+"F0.wireOp",EDGE,"E25.0"),sQuery(id+"F0.wireOp",EDGE,"E25.1"),sQuery(id+"F0.wireOp",EDGE,"E25.2"),sQuery(id+"F0.wireOp",EDGE,"E25.3"),sQuery(id+"F0.wireOp",EDGE,"E25.4"),sQuery(id+"F0.wireOp",EDGE,"E25.5"),sQuery(id+"F0.wireOp",EDGE,"E25.6"),sQuery(id+"F0.wireOp",EDGE,"E25.7")])],"isStart":false});
            extrude(context, id + "F17", {"entities" : qUnion([Q0, Q1]), "endBound" : BoundingType.UP_TO_SURFACE, "depth" : 25 * mm, "endBoundEntityFace" : qUnion([Q2]), "offsetDistance" : 25 * mm});
        }
    });
